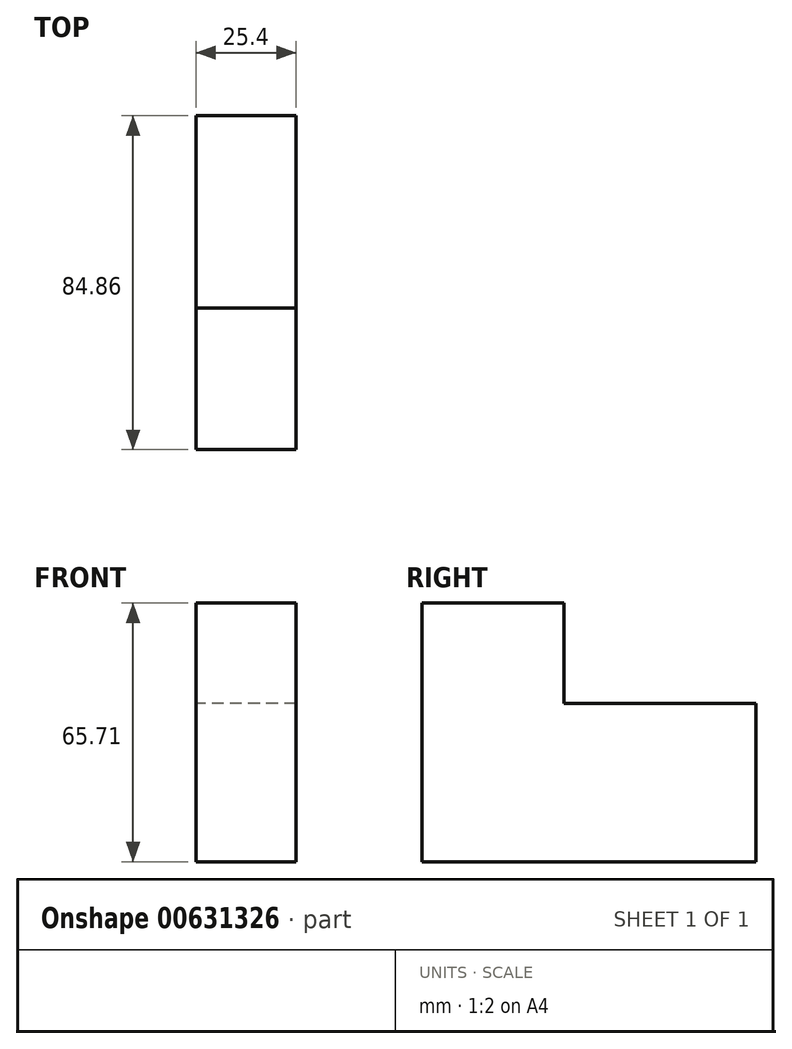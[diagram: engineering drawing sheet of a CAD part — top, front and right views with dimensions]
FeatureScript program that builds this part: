
annotation { "Feature Type Name" : "Feature", "Feature Type Description" : "" }
export const myFeature = defineFeature(function(context is Context, id is Id, definition is map)
    precondition{}
    {
        {
            var Q0;
            Q0=qCreatedBy(makeId("Right.planeOp"),FACE);
            var sketch = newSketch(context, id + "F0", { "sketchPlane" : qUnion([Q0])});
            skLineSegment(sketch, "E0.bottom", {"start": v(0, 0) * mm, "end": v(84.86, 0) * mm});
            skLineSegment(sketch, "E0.top", {"start": v(0, 40.23) * mm, "end": v(84.86, 40.23) * mm});
            skLineSegment(sketch, "E0.left", {"start": v(0, 0) * mm, "end": v(0, 40.23) * mm});
            skLineSegment(sketch, "E0.right", {"start": v(84.86, 0) * mm, "end": v(84.86, 40.23) * mm});
            skLineSegment(sketch, "E1.bottom", {"start": v(0, 40.23) * mm, "end": v(36.02, 40.23) * mm});
            skLineSegment(sketch, "E1.top", {"start": v(0, 65.7) * mm, "end": v(36.02, 65.7) * mm});
            skLineSegment(sketch, "E1.left", {"start": v(0, 40.23) * mm, "end": v(0, 65.7) * mm});
            skLineSegment(sketch, "E1.right", {"start": v(36.02, 40.23) * mm, "end": v(36.02, 65.7) * mm});
            skSolve(sketch);
        }
        {
            var Q0;
            Q0 = qSketchRegion(id + "F0", true);
            extrude(context, id + "F1", {"entities" : qUnion([Q0]), "depth" : 25.4 * mm, "offsetDistance" : 25.4 * mm});
        }
    });
